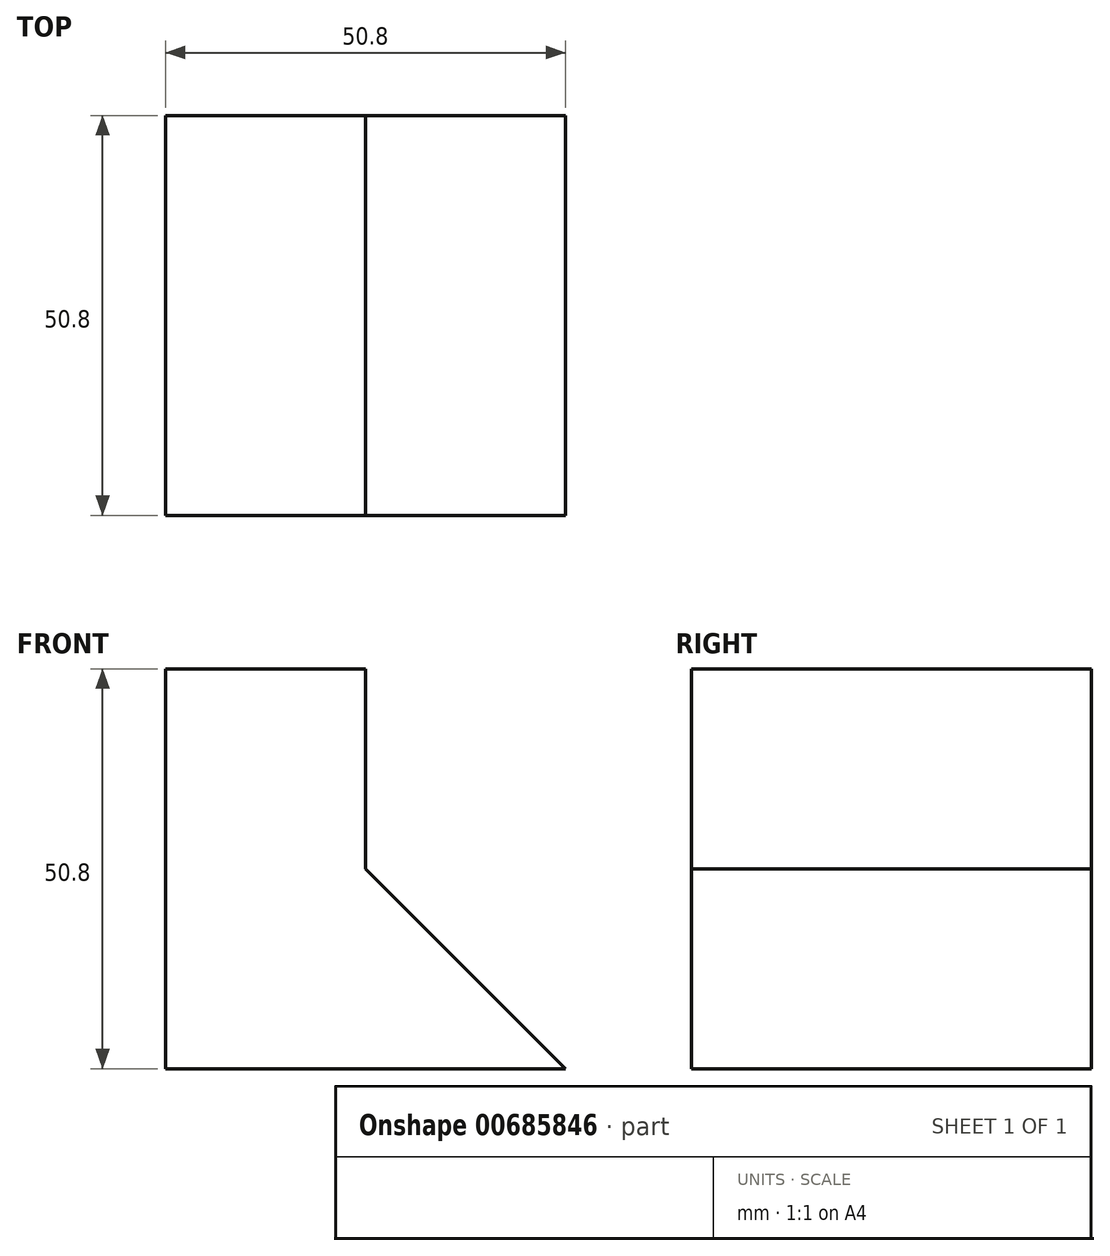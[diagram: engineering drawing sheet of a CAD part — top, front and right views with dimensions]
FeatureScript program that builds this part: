
annotation { "Feature Type Name" : "Feature", "Feature Type Description" : "" }
export const myFeature = defineFeature(function(context is Context, id is Id, definition is map)
    precondition{}
    {
        {
            var Q0;
            Q0=qCreatedBy(makeId("Front.planeOp"),FACE);
            var sketch = newSketch(context, id + "F0", { "sketchPlane" : qUnion([Q0])});
            skLineSegment(sketch, "E0", {"start": v(0, 0) * mm, "end": v(-50.8, 0) * mm});
            skLineSegment(sketch, "E1", {"start": v(-50.8, 0) * mm, "end": v(-50.8, 50.8) * mm});
            skLineSegment(sketch, "E2", {"start": v(-50.8, 50.8) * mm, "end": v(-25.4, 50.8) * mm});
            skLineSegment(sketch, "E3", {"start": v(-25.4, 50.8) * mm, "end": v(-25.4, 25.4) * mm});
            skLineSegment(sketch, "E4", {"start": v(-25.4, 25.4) * mm, "end": v(0, 0) * mm});
            skSolve(sketch);
        }
        {
            var Q0;
            Q0 = qSketchRegion(id + "F0", true);
            extrude(context, id + "F1", {"entities" : qUnion([Q0]), "depth" : 50.8 * mm, "offsetDistance" : 25.4 * mm});
        }
    });
